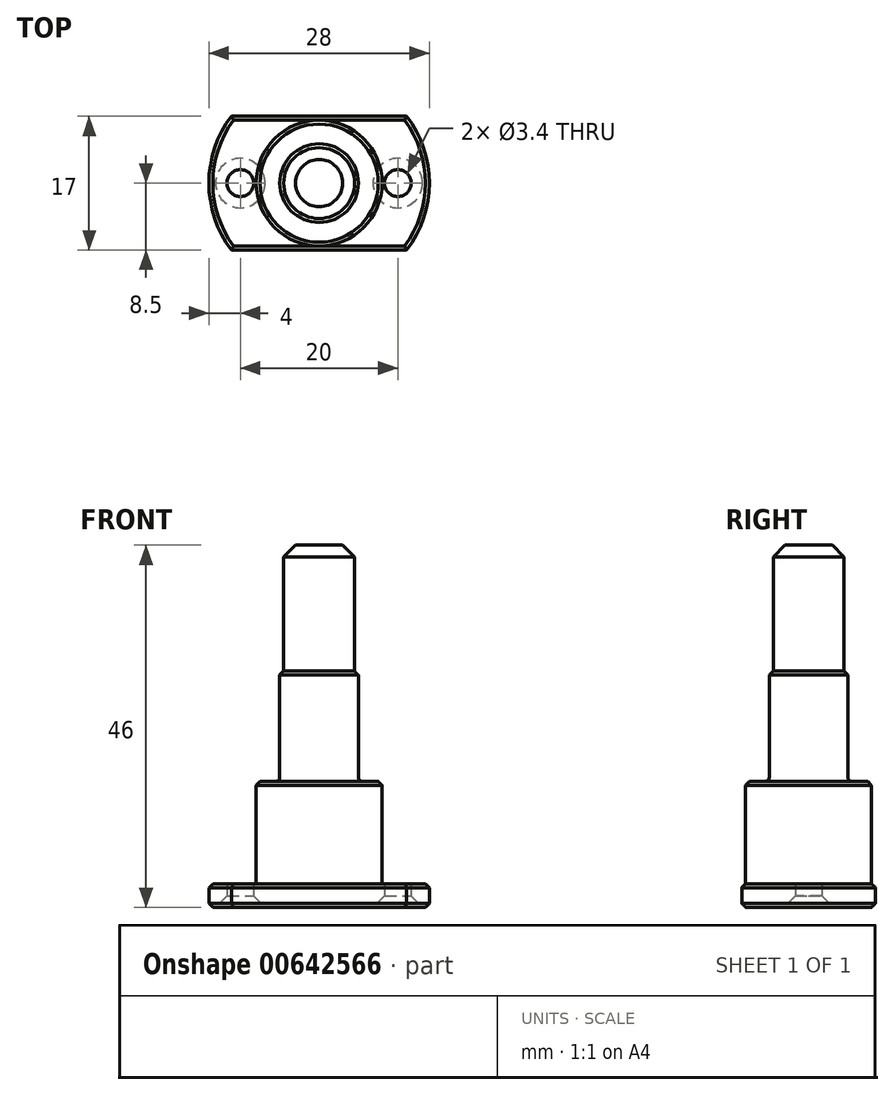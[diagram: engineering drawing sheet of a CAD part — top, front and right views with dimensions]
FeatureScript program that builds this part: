
annotation { "Feature Type Name" : "Feature", "Feature Type Description" : "" }
export const myFeature = defineFeature(function(context is Context, id is Id, definition is map)
    precondition{}
    {
        {
            var Q0;
            Q0=qCreatedBy(makeId("Top.planeOp"),FACE);
            var sketch = newSketch(context, id + "F0", { "sketchPlane" : qUnion([Q0])});
            skArc(sketch, "E0", {"start": v(-11.12, 8.5) * mm, "mid": v(-14, 0) * mm, "end": v(-11.12, -8.5) * mm});
            skLineSegment(sketch, "E1", {"start": v(-11.12, 8.5) * mm, "end": v(11.12, 8.5) * mm});
            skLineSegment(sketch, "E2.MirrorCS", {"start": v(-11.12, -8.5) * mm, "end": v(11.12, -8.5) * mm});
            skArc(sketch, "E3.trimOffspring", {"start": v(11.12, -8.5) * mm, "mid": v(14, 0) * mm, "end": v(11.12, 8.5) * mm});
            skSolve(sketch);
        }
        {
            var Q0;
            Q0 = qSketchRegion(id + "F0", true);
            extrude(context, id + "F1", {"entities" : qUnion([Q0]), "depth" : 3 * mm, "offsetDistance" : 25 * mm});
        }
        {
            var Q0;
            Q0=qCreatedBy(makeId("Top.planeOp"),FACE);
            var sketch = newSketch(context, id + "F2", { "sketchPlane" : qUnion([Q0])});
            skCircle(sketch, "E4", {"center": v(0, 0) * mm, "radius": 8 * mm});
            skSolve(sketch);
        }
        {
            var Q0;
            Q0 = qSketchRegion(id + "F2", true);
            extrude(context, id + "F3", {"entities" : qUnion([Q0]), "operationType" : NewBodyOperationType.ADD, "depth" : 16 * mm, "offsetDistance" : 25 * mm});
        }
        {
            var Q0;
            Q0=qCreatedBy(makeId("Top.planeOp"),FACE);
            var sketch = newSketch(context, id + "F4", { "sketchPlane" : qUnion([Q0])});
            skCircle(sketch, "E5", {"center": v(0, 0) * mm, "radius": 5 * mm});
            skSolve(sketch);
        }
        {
            var Q0;
            Q0 = qSketchRegion(id + "F4", true);
            extrude(context, id + "F5", {"entities" : qUnion([Q0]), "operationType" : NewBodyOperationType.ADD, "depth" : 30 * mm, "offsetDistance" : 25 * mm});
        }
        {
            var Q0;
            Q0=qCreatedBy(makeId("Top.planeOp"),FACE);
            var sketch = newSketch(context, id + "F6", { "sketchPlane" : qUnion([Q0])});
            skCircle(sketch, "E6", {"center": v(0, 0) * mm, "radius": 4.5 * mm});
            skSolve(sketch);
        }
        {
            var Q0;
            Q0 = qSketchRegion(id + "F6", true);
            extrude(context, id + "F7", {"entities" : qUnion([Q0]), "operationType" : NewBodyOperationType.ADD, "depth" : 46 * mm, "offsetDistance" : 25 * mm});
        }
        {
            var Q0;
            Q0=makeQuery(id+"F1.opExtrude","CAP_FACE",FACE,{"disambiguationData":[OSD([sQuery(id+"F0.wireOp",EDGE,"E0"),sQuery(id+"F0.wireOp",EDGE,"E1"),sQuery(id+"F0.wireOp",EDGE,"E2.MirrorCS"),sQuery(id+"F0.wireOp",EDGE,"E3.trimOffspring")])],"isStart":true});
            var sketch = newSketch(context, id + "F8", { "sketchPlane" : qUnion([Q0])});
            skPoint(sketch, "E7", {"position": v(-10, 0) * mm});
            skSolve(sketch);
        }
        {
            var Q0;
            Q0=makeQuery(id+"F8.imprint","IMPRINT",FACE,{"disambiguationData":[TD([[makeQuery(id+"F8.imprint","IMPRINT",EDGE,{"derivedFrom":makeQuery(id+"F1.opExtrude","CAP_EDGE",EDGE,{"disambiguationData":[OSD([sQuery(id+"F0.wireOp",EDGE,"E0")])],"isStart":true})}),-1.0]])]});
            var sketch = newSketch(context, id + "F9", { "sketchPlane" : qUnion([Q0])});
            skPoint(sketch, "E8", {"position": v(10, 0) * mm});
            skSolve(sketch);
        }
        {
            var Q0;
            Q0=sQuery(id+"F8.wireOp",VERTEX,"E7");
            var Q1;
            Q1=makeQuery(id+"F1.opExtrude","SWEPT_BODY",BODY,{"disambiguationData":[OSD([sQuery(id+"F0.wireOp",EDGE,"E0"),sQuery(id+"F0.wireOp",EDGE,"E1"),sQuery(id+"F0.wireOp",EDGE,"E2.MirrorCS"),sQuery(id+"F0.wireOp",EDGE,"E3.trimOffspring")])]});
            hole(context, id + "F10", {"style" : HoleStyle.C_SINK, "endStyle" : HoleEndStyle.THROUGH, "holeDiameter" : 3.4 * mm, "cSinkDiameter" : 6.3 * mm, "cSinkAngle" : 90 * degree, "majorDiameter" : 5 * mm, "isTappedThrough" : true, "tappedDepth" : 12 * mm, "tapClearance" : 3, "locations" : qUnion([Q0]), "scope" : qUnion([Q1])});
        }
        {
            var Q0;
            Q0=sQuery(id+"F9.wireOp",VERTEX,"E8");
            var Q1;
            Q1=makeQuery(id+"F1.opExtrude","SWEPT_BODY",BODY,{"disambiguationData":[OSD([sQuery(id+"F0.wireOp",EDGE,"E0"),sQuery(id+"F0.wireOp",EDGE,"E1"),sQuery(id+"F0.wireOp",EDGE,"E2.MirrorCS"),sQuery(id+"F0.wireOp",EDGE,"E3.trimOffspring")])]});
            hole(context, id + "F11", {"style" : HoleStyle.C_SINK, "endStyle" : HoleEndStyle.THROUGH, "holeDiameter" : 3.4 * mm, "cSinkDiameter" : 6.3 * mm, "cSinkAngle" : 90 * degree, "majorDiameter" : 5 * mm, "isTappedThrough" : true, "tappedDepth" : 12 * mm, "tapClearance" : 3, "locations" : qUnion([Q0]), "scope" : qUnion([Q1])});
        }
        {
            var Q0;
            Q0=makeQuery(id+"F7.opExtrude","CAP_FACE",FACE,{"disambiguationData":[OSD([sQuery(id+"F6.wireOp",EDGE,"E6")])],"isStart":false});
            chamfer(context, id + "F12", {"entities" : qUnion([Q0]), "chamferType" : ChamferType.OFFSET_ANGLE, "width" : 1.5 * mm, "oppositeDirection" : false, "angle" : 45 * degree, "tangentPropagation" : true});
        }
        {
            var Q0;
            Q0=makeQuery(id+"F5.opExtrude","CAP_EDGE",EDGE,{"disambiguationData":[OSD([sQuery(id+"F4.wireOp",EDGE,"E5")])],"isStart":false});
            chamfer(context, id + "F13", {"entities" : qUnion([Q0]), "chamferType" : ChamferType.OFFSET_ANGLE, "width" : 0.5 * mm, "oppositeDirection" : false, "angle" : 45 * degree, "tangentPropagation" : true});
        }
        {
            var Q0;
            Q0=makeQuery(id+"F3.opExtrude","CAP_EDGE",EDGE,{"disambiguationData":[OSD([sQuery(id+"F2.wireOp",EDGE,"E4")])],"isStart":false});
            chamfer(context, id + "F14", {"entities" : qUnion([Q0]), "chamferType" : ChamferType.OFFSET_ANGLE, "width" : 0.5 * mm, "oppositeDirection" : false, "angle" : 45 * degree, "tangentPropagation" : true});
        }
        {
            var Q0;
            Q0=makeQuery(id+"F1.opExtrude","CAP_EDGE",EDGE,{"disambiguationData":[OSD([sQuery(id+"F0.wireOp",EDGE,"E2.MirrorCS")])],"isStart":false});
            chamfer(context, id + "F15", {"entities" : qUnion([Q0]), "chamferType" : ChamferType.OFFSET_ANGLE, "width" : 0.5 * mm, "oppositeDirection" : false, "angle" : 45 * degree, "tangentPropagation" : true});
        }
        {
            var Q0;
            Q0=makeQuery(id+"F1.opExtrude","CAP_EDGE",EDGE,{"disambiguationData":[OSD([sQuery(id+"F0.wireOp",EDGE,"E0")])],"isStart":false});
            chamfer(context, id + "F16", {"entities" : qUnion([Q0]), "chamferType" : ChamferType.OFFSET_ANGLE, "width" : 0.5 * mm, "oppositeDirection" : false, "angle" : 45 * degree, "tangentPropagation" : true});
        }
        {
            var Q0;
            Q0=makeQuery(id+"F1.opExtrude","CAP_EDGE",EDGE,{"disambiguationData":[OSD([sQuery(id+"F0.wireOp",EDGE,"E1")])],"isStart":false});
            chamfer(context, id + "F17", {"entities" : qUnion([Q0]), "chamferType" : ChamferType.OFFSET_ANGLE, "width" : 0.5 * mm, "oppositeDirection" : false, "angle" : 45 * degree, "tangentPropagation" : true});
        }
        {
            var Q0;
            Q0=makeQuery(id+"F1.opExtrude","CAP_EDGE",EDGE,{"disambiguationData":[OSD([sQuery(id+"F0.wireOp",EDGE,"E3.trimOffspring")])],"isStart":false});
            chamfer(context, id + "F18", {"entities" : qUnion([Q0]), "chamferType" : ChamferType.OFFSET_ANGLE, "width" : 0.5 * mm, "oppositeDirection" : false, "angle" : 45 * degree, "tangentPropagation" : true});
        }
        {
            var Q0;
            Q0=makeQuery(id+"F5.boolean.opBoolean","INTERSECT",EDGE,{"derivedFrom":[makeQuery(id+"F3.opExtrude","CAP_FACE",FACE,{"disambiguationData":[OSD([sQuery(id+"F2.wireOp",EDGE,"E4")])],"isStart":false}),makeQuery(id+"F5.opExtrude","SWEPT_FACE",FACE,{"disambiguationData":[OSD([sQuery(id+"F4.wireOp",EDGE,"E5")])]})]});
            fillet(context, id + "F19", {"entities" : qUnion([Q0]), "radius" : 0.5 * mm, "tangentPropagation" : true, "allowEdgeOverflow" : false});
        }
        {
            var Q0;
            Q0=makeQuery(id+"F1.opExtrude","CAP_EDGE",EDGE,{"disambiguationData":[OSD([sQuery(id+"F0.wireOp",EDGE,"E2.MirrorCS")])],"isStart":true});
            chamfer(context, id + "F20", {"entities" : qUnion([Q0]), "chamferType" : ChamferType.OFFSET_ANGLE, "width" : 0.5 * mm, "oppositeDirection" : false, "angle" : 45 * degree, "tangentPropagation" : true});
        }
        {
            var Q0;
            Q0=makeQuery(id+"F1.opExtrude","CAP_EDGE",EDGE,{"disambiguationData":[OSD([sQuery(id+"F0.wireOp",EDGE,"E0")])],"isStart":true});
            chamfer(context, id + "F21", {"entities" : qUnion([Q0]), "chamferType" : ChamferType.OFFSET_ANGLE, "width" : 0.5 * mm, "oppositeDirection" : false, "angle" : 45 * degree, "tangentPropagation" : true});
        }
        {
            var Q0;
            Q0=makeQuery(id+"F1.opExtrude","CAP_EDGE",EDGE,{"disambiguationData":[OSD([sQuery(id+"F0.wireOp",EDGE,"E1")])],"isStart":true});
            chamfer(context, id + "F22", {"entities" : qUnion([Q0]), "chamferType" : ChamferType.OFFSET_ANGLE, "width" : 0.5 * mm, "oppositeDirection" : false, "angle" : 45 * degree, "tangentPropagation" : true});
        }
        {
            var Q0;
            Q0=makeQuery(id+"F1.opExtrude","CAP_EDGE",EDGE,{"disambiguationData":[OSD([sQuery(id+"F0.wireOp",EDGE,"E3.trimOffspring")])],"isStart":true});
            chamfer(context, id + "F23", {"entities" : qUnion([Q0]), "chamferType" : ChamferType.OFFSET_ANGLE, "width" : 0.5 * mm, "oppositeDirection" : false, "angle" : 45 * degree, "tangentPropagation" : true});
        }
    });
